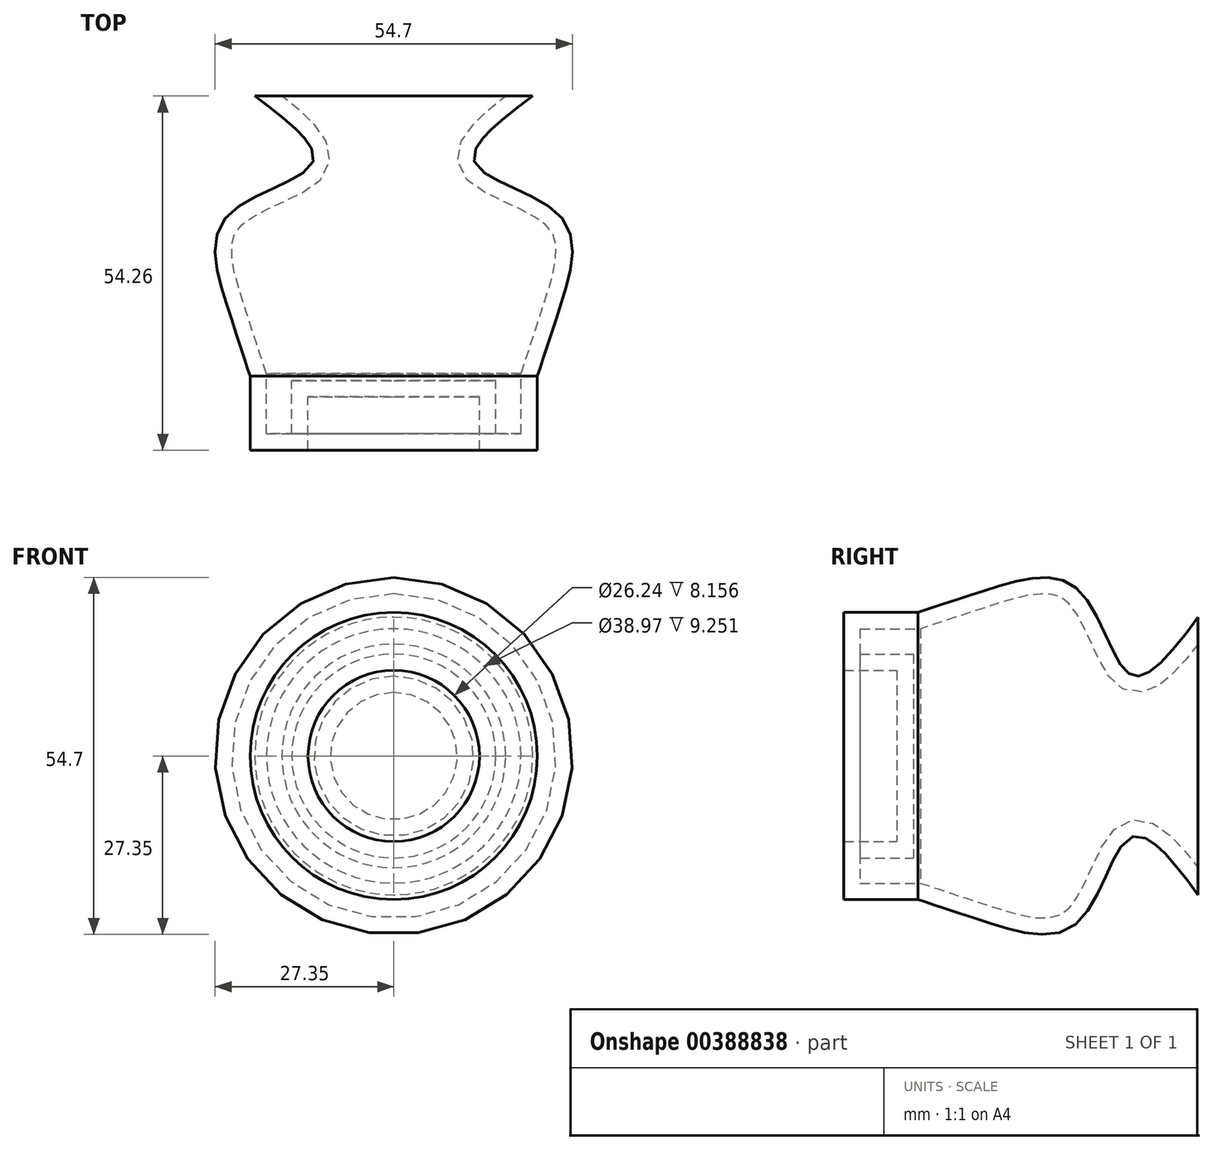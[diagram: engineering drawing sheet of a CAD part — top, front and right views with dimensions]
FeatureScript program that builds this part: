
annotation { "Feature Type Name" : "Feature", "Feature Type Description" : "" }
export const myFeature = defineFeature(function(context is Context, id is Id, definition is map)
    precondition{}
    {
        {
            var Q0;
            Q0=qCreatedBy(makeId("Top.planeOp"),FACE);
            var sketch = newSketch(context, id + "F0", { "sketchPlane" : qUnion([Q0])});
            skLineSegment(sketch, "E0", {"start": v(0, 0) * mm, "end": v(0, -46.1) * mm});
            skLineSegment(sketch, "E1", {"start": v(0, -46.1) * mm, "end": v(13.12, -46.1) * mm});
            skLineSegment(sketch, "E2", {"start": v(13.12, -46.1) * mm, "end": v(13.12, -54.26) * mm});
            skLineSegment(sketch, "E3", {"start": v(13.12, -54.26) * mm, "end": v(21.99, -54.26) * mm});
            skLineSegment(sketch, "E4", {"start": v(21.99, -54.26) * mm, "end": v(21.99, -42.9) * mm});
            skLineSegment(sketch, "E5", {"start": v(0, 0) * mm, "end": v(21.28, 0) * mm});
            skFitSpline(sketch, "E6", {"points": [v(21.28, 0) * mm, v(12.43, -10.27) * mm, v(25.7, -18.62) * mm, v(25.55, -32.03) * mm, v(21.99, -42.9) * mm], "startDerivative": vector(-60.54, -45.31) * mm, "endDerivative": vector(-14.54, -43.83) * mm});
            skSolve(sketch);
        }
        {
            var Q0;
            Q0 = qSketchRegion(id + "F0", true);
            var Q1;
            Q1=sQuery(id+"F0.wireOp",EDGE,"E0");
            revolve(context, id + "F1", {"entities" : qUnion([Q0]), "axis" : qUnion([Q1]), "revolveType" : RevolveType.FULL});
        }
        {
            var Q0;
            Q0=makeQuery(id+"F1.opRevolve","SWEPT_FACE",FACE,{"disambiguationData":[OSD([sQuery(id+"F0.wireOp",EDGE,"E5")])]});
            shell(context, id + "F2", {"entities" : qUnion([Q0]), "thickness" : 2.5 * mm});
        }
    });
